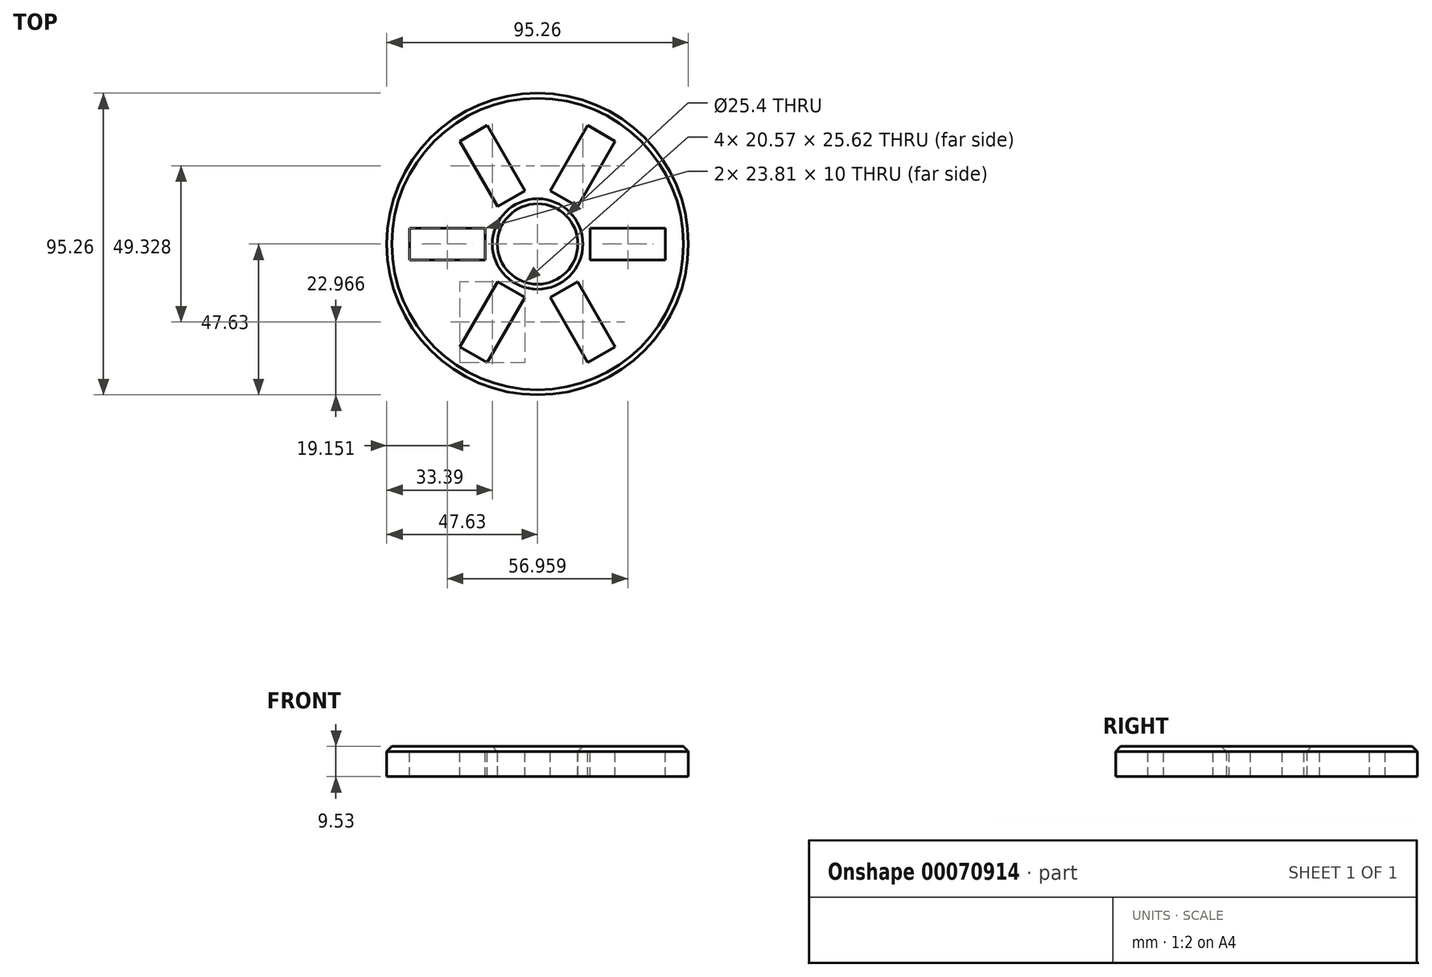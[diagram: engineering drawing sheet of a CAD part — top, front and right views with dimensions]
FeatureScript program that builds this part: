
annotation { "Feature Type Name" : "Feature", "Feature Type Description" : "" }
export const myFeature = defineFeature(function(context is Context, id is Id, definition is map)
    precondition{}
    {
        {
            var Q0;
            Q0=qCreatedBy(makeId("Top.planeOp"),FACE);
            var sketch = newSketch(context, id + "F0", { "sketchPlane" : qUnion([Q0])});
            skCircle(sketch, "E0", {"center": v(0, 0) * mm, "radius": 47.63 * mm});
            skCircle(sketch, "E1", {"center": v(0, 0) * mm, "radius": 12.7 * mm});
            skSolve(sketch);
        }
        {
            var Q0;
            Q0=makeQuery(id+"F0.imprint","IMPRINT",FACE,{"disambiguationData":[TD([[makeQuery(id+"F0.imprint","IMPRINT",EDGE,{"derivedFrom":sQuery(id+"F0.wireOp",EDGE,"E0")}),1.0]])]});
            extrude(context, id + "F1", {"entities" : qUnion([Q0]), "depth" : 9.52 * mm});
        }
        {
            var Q0;
            Q0=makeQuery(id+"F1.opExtrude","CAP_FACE",FACE,{"disambiguationData":[OSD([sQuery(id+"F0.wireOp",EDGE,"E0"),sQuery(id+"F0.wireOp",EDGE,"E1")])],"isStart":false});
            var sketch = newSketch(context, id + "F2", { "sketchPlane" : qUnion([Q0])});
            skLineSegment(sketch, "E2.rect.bottom", {"start": v(-16.57, -5) * mm, "end": v(-40.39, -5) * mm});
            skLineSegment(sketch, "E2.rect.top", {"start": v(-16.57, 5) * mm, "end": v(-40.39, 5) * mm});
            skLineSegment(sketch, "E2.rect.left", {"start": v(-16.57, -5) * mm, "end": v(-16.57, 5) * mm});
            skLineSegment(sketch, "E2.rect.right", {"start": v(-40.39, -5) * mm, "end": v(-40.39, 5) * mm});
            skPoint(sketch, "E2.rect.middle", {"position": v(-28.48, 0) * mm});
            skLineSegment(sketch, "E3", {"start": v(-47.63, 0) * mm, "end": v(-12.7, 0) * mm, "construction": true});
            skPoint(sketch, "E3.startSnap0", {"position": v(-40.39, 0) * mm});
            skPoint(sketch, "E3.endSnap0", {"position": v(-16.57, 0) * mm});
            skLineSegment(sketch, "E4.1.0", {"start": v(-12.62, -11.85) * mm, "end": v(-24.52, -32.48) * mm});
            skLineSegment(sketch, "E4.1.1", {"start": v(-3.96, -16.85) * mm, "end": v(-15.86, -37.48) * mm});
            skLineSegment(sketch, "E4.1.2", {"start": v(-3.96, -16.85) * mm, "end": v(-12.62, -11.85) * mm});
            skLineSegment(sketch, "E4.1.3", {"start": v(-15.86, -37.48) * mm, "end": v(-24.52, -32.48) * mm});
            skLineSegment(sketch, "E4.2.0", {"start": v(3.96, -16.85) * mm, "end": v(15.86, -37.48) * mm});
            skLineSegment(sketch, "E4.2.1", {"start": v(12.62, -11.85) * mm, "end": v(24.52, -32.48) * mm});
            skLineSegment(sketch, "E4.2.2", {"start": v(12.62, -11.85) * mm, "end": v(3.96, -16.85) * mm});
            skLineSegment(sketch, "E4.2.3", {"start": v(24.52, -32.48) * mm, "end": v(15.86, -37.48) * mm});
            skLineSegment(sketch, "E4.3.0", {"start": v(16.57, -5) * mm, "end": v(40.39, -5) * mm});
            skLineSegment(sketch, "E4.3.1", {"start": v(16.57, 5) * mm, "end": v(40.39, 5) * mm});
            skLineSegment(sketch, "E4.3.2", {"start": v(16.57, 5) * mm, "end": v(16.57, -5) * mm});
            skLineSegment(sketch, "E4.3.3", {"start": v(40.39, 5) * mm, "end": v(40.39, -5) * mm});
            skLineSegment(sketch, "E4.4.0", {"start": v(12.62, 11.85) * mm, "end": v(24.52, 32.48) * mm});
            skLineSegment(sketch, "E4.4.1", {"start": v(3.96, 16.85) * mm, "end": v(15.86, 37.48) * mm});
            skLineSegment(sketch, "E4.4.2", {"start": v(3.96, 16.85) * mm, "end": v(12.62, 11.85) * mm});
            skLineSegment(sketch, "E4.4.3", {"start": v(15.86, 37.48) * mm, "end": v(24.52, 32.48) * mm});
            skLineSegment(sketch, "E4.5.0", {"start": v(-3.96, 16.85) * mm, "end": v(-15.86, 37.48) * mm});
            skLineSegment(sketch, "E4.5.1", {"start": v(-12.62, 11.85) * mm, "end": v(-24.52, 32.48) * mm});
            skLineSegment(sketch, "E4.5.2", {"start": v(-12.62, 11.85) * mm, "end": v(-3.96, 16.85) * mm});
            skLineSegment(sketch, "E4.5.3", {"start": v(-24.52, 32.48) * mm, "end": v(-15.86, 37.48) * mm});
            skPoint(sketch, "E4.center", {"position": v(0, 0) * mm});
            skSolve(sketch);
        }
        {
            var Q0;
            Q0=makeQuery(id+"F2.imprint","IMPRINT",FACE,{"disambiguationData":[TD([[makeQuery(id+"F2.imprint","IMPRINT",EDGE,{"derivedFrom":sQuery(id+"F2.wireOp",EDGE,"E2.rect.bottom")}),-1.0]])]});
            var Q1;
            Q1=makeQuery(id+"F2.imprint","IMPRINT",FACE,{"disambiguationData":[TD([[makeQuery(id+"F2.imprint","IMPRINT",EDGE,{"derivedFrom":sQuery(id+"F2.wireOp",EDGE,"E4.5.0")}),1.0]])]});
            var Q2;
            Q2=makeQuery(id+"F2.imprint","IMPRINT",FACE,{"disambiguationData":[TD([[makeQuery(id+"F2.imprint","IMPRINT",EDGE,{"derivedFrom":sQuery(id+"F2.wireOp",EDGE,"E4.4.0")}),1.0]])]});
            var Q3;
            Q3=makeQuery(id+"F2.imprint","IMPRINT",FACE,{"disambiguationData":[TD([[makeQuery(id+"F2.imprint","IMPRINT",EDGE,{"derivedFrom":sQuery(id+"F2.wireOp",EDGE,"E4.3.0")}),1.0]])]});
            var Q4;
            Q4=makeQuery(id+"F2.imprint","IMPRINT",FACE,{"disambiguationData":[TD([[makeQuery(id+"F2.imprint","IMPRINT",EDGE,{"derivedFrom":sQuery(id+"F2.wireOp",EDGE,"E4.2.0")}),1.0]])]});
            var Q5;
            Q5=makeQuery(id+"F2.imprint","IMPRINT",FACE,{"disambiguationData":[TD([[makeQuery(id+"F2.imprint","IMPRINT",EDGE,{"derivedFrom":sQuery(id+"F2.wireOp",EDGE,"E4.1.0")}),1.0]])]});
            extrude(context, id + "F3", {"entities" : qUnion([Q0, Q1, Q2, Q3, Q4, Q5]), "operationType" : NewBodyOperationType.REMOVE, "endBound" : BoundingType.THROUGH_ALL, "oppositeDirection" : true, "depth" : 6.35 * mm});
        }
        {
            var Q0;
            Q0=makeQuery(id+"F3.boolean.opBoolean","COPY",EDGE,{"derivedFrom":makeQuery(id+"F3.opExtrude","CAP_EDGE",EDGE,{"disambiguationData":[OSD([sQuery(id+"F2.wireOp",EDGE,"E2.rect.top")])],"isStart":true})});
            var Q1;
            Q1=makeQuery(id+"F3.boolean.opBoolean","COPY",EDGE,{"derivedFrom":makeQuery(id+"F3.opExtrude","CAP_EDGE",EDGE,{"disambiguationData":[OSD([sQuery(id+"F2.wireOp",EDGE,"E2.rect.right")])],"isStart":true})});
            var Q2;
            Q2=makeQuery(id+"F3.boolean.opBoolean","COPY",EDGE,{"derivedFrom":makeQuery(id+"F3.opExtrude","CAP_EDGE",EDGE,{"disambiguationData":[OSD([sQuery(id+"F2.wireOp",EDGE,"E2.rect.bottom")])],"isStart":true})});
            var Q3;
            Q3=makeQuery(id+"F3.boolean.opBoolean","COPY",EDGE,{"derivedFrom":makeQuery(id+"F3.opExtrude","CAP_EDGE",EDGE,{"disambiguationData":[OSD([sQuery(id+"F2.wireOp",EDGE,"E2.rect.left")])],"isStart":true})});
            var Q4;
            Q4=makeQuery(id+"F1.opExtrude","CAP_EDGE",EDGE,{"disambiguationData":[OSD([sQuery(id+"F0.wireOp",EDGE,"E1")])],"isStart":false});
            var Q5;
            Q5=makeQuery(id+"F3.boolean.opBoolean","COPY",EDGE,{"derivedFrom":makeQuery(id+"F3.opExtrude","CAP_EDGE",EDGE,{"disambiguationData":[OSD([sQuery(id+"F2.wireOp",EDGE,"E4.5.2")])],"isStart":true})});
            var Q6;
            Q6=makeQuery(id+"F3.boolean.opBoolean","COPY",EDGE,{"derivedFrom":makeQuery(id+"F3.opExtrude","CAP_EDGE",EDGE,{"disambiguationData":[OSD([sQuery(id+"F2.wireOp",EDGE,"E4.5.1")])],"isStart":true})});
            var Q7;
            Q7=makeQuery(id+"F3.boolean.opBoolean","COPY",EDGE,{"derivedFrom":makeQuery(id+"F3.opExtrude","CAP_EDGE",EDGE,{"disambiguationData":[OSD([sQuery(id+"F2.wireOp",EDGE,"E4.5.0")])],"isStart":true})});
            var Q8;
            Q8=makeQuery(id+"F3.boolean.opBoolean","COPY",EDGE,{"derivedFrom":makeQuery(id+"F3.opExtrude","CAP_EDGE",EDGE,{"disambiguationData":[OSD([sQuery(id+"F2.wireOp",EDGE,"E4.5.3")])],"isStart":true})});
            var Q9;
            Q9=makeQuery(id+"F3.boolean.opBoolean","COPY",EDGE,{"derivedFrom":makeQuery(id+"F3.opExtrude","CAP_EDGE",EDGE,{"disambiguationData":[OSD([sQuery(id+"F2.wireOp",EDGE,"E4.4.1")])],"isStart":true})});
            var Q10;
            Q10=makeQuery(id+"F3.boolean.opBoolean","COPY",EDGE,{"derivedFrom":makeQuery(id+"F3.opExtrude","CAP_EDGE",EDGE,{"disambiguationData":[OSD([sQuery(id+"F2.wireOp",EDGE,"E4.4.3")])],"isStart":true})});
            var Q11;
            Q11=makeQuery(id+"F3.boolean.opBoolean","COPY",EDGE,{"derivedFrom":makeQuery(id+"F3.opExtrude","CAP_EDGE",EDGE,{"disambiguationData":[OSD([sQuery(id+"F2.wireOp",EDGE,"E4.4.2")])],"isStart":true})});
            var Q12;
            Q12=makeQuery(id+"F3.boolean.opBoolean","COPY",EDGE,{"derivedFrom":makeQuery(id+"F3.opExtrude","CAP_EDGE",EDGE,{"disambiguationData":[OSD([sQuery(id+"F2.wireOp",EDGE,"E4.4.0")])],"isStart":true})});
            var Q13;
            Q13=makeQuery(id+"F3.boolean.opBoolean","COPY",EDGE,{"derivedFrom":makeQuery(id+"F3.opExtrude","CAP_EDGE",EDGE,{"disambiguationData":[OSD([sQuery(id+"F2.wireOp",EDGE,"E4.3.2")])],"isStart":true})});
            var Q14;
            Q14=makeQuery(id+"F3.boolean.opBoolean","COPY",EDGE,{"derivedFrom":makeQuery(id+"F3.opExtrude","CAP_EDGE",EDGE,{"disambiguationData":[OSD([sQuery(id+"F2.wireOp",EDGE,"E4.3.1")])],"isStart":true})});
            var Q15;
            Q15=makeQuery(id+"F3.boolean.opBoolean","COPY",EDGE,{"derivedFrom":makeQuery(id+"F3.opExtrude","CAP_EDGE",EDGE,{"disambiguationData":[OSD([sQuery(id+"F2.wireOp",EDGE,"E4.3.3")])],"isStart":true})});
            var Q16;
            Q16=makeQuery(id+"F3.boolean.opBoolean","COPY",EDGE,{"derivedFrom":makeQuery(id+"F3.opExtrude","CAP_EDGE",EDGE,{"disambiguationData":[OSD([sQuery(id+"F2.wireOp",EDGE,"E4.3.0")])],"isStart":true})});
            var Q17;
            Q17=makeQuery(id+"F3.boolean.opBoolean","COPY",EDGE,{"derivedFrom":makeQuery(id+"F3.opExtrude","CAP_EDGE",EDGE,{"disambiguationData":[OSD([sQuery(id+"F2.wireOp",EDGE,"E4.2.1")])],"isStart":true})});
            var Q18;
            Q18=makeQuery(id+"F3.boolean.opBoolean","COPY",EDGE,{"derivedFrom":makeQuery(id+"F3.opExtrude","CAP_EDGE",EDGE,{"disambiguationData":[OSD([sQuery(id+"F2.wireOp",EDGE,"E4.2.2")])],"isStart":true})});
            var Q19;
            Q19=makeQuery(id+"F3.boolean.opBoolean","COPY",EDGE,{"derivedFrom":makeQuery(id+"F3.opExtrude","CAP_EDGE",EDGE,{"disambiguationData":[OSD([sQuery(id+"F2.wireOp",EDGE,"E4.2.0")])],"isStart":true})});
            var Q20;
            Q20=makeQuery(id+"F3.boolean.opBoolean","COPY",EDGE,{"derivedFrom":makeQuery(id+"F3.opExtrude","CAP_EDGE",EDGE,{"disambiguationData":[OSD([sQuery(id+"F2.wireOp",EDGE,"E4.2.3")])],"isStart":true})});
            var Q21;
            Q21=makeQuery(id+"F3.boolean.opBoolean","COPY",EDGE,{"derivedFrom":makeQuery(id+"F3.opExtrude","CAP_EDGE",EDGE,{"disambiguationData":[OSD([sQuery(id+"F2.wireOp",EDGE,"E4.1.1")])],"isStart":true})});
            var Q22;
            Q22=makeQuery(id+"F3.boolean.opBoolean","COPY",EDGE,{"derivedFrom":makeQuery(id+"F3.opExtrude","CAP_EDGE",EDGE,{"disambiguationData":[OSD([sQuery(id+"F2.wireOp",EDGE,"E4.1.3")])],"isStart":true})});
            var Q23;
            Q23=makeQuery(id+"F3.boolean.opBoolean","COPY",EDGE,{"derivedFrom":makeQuery(id+"F3.opExtrude","CAP_EDGE",EDGE,{"disambiguationData":[OSD([sQuery(id+"F2.wireOp",EDGE,"E4.1.0")])],"isStart":true})});
            var Q24;
            Q24=makeQuery(id+"F3.boolean.opBoolean","COPY",EDGE,{"derivedFrom":makeQuery(id+"F3.opExtrude","CAP_EDGE",EDGE,{"disambiguationData":[OSD([sQuery(id+"F2.wireOp",EDGE,"E4.1.2")])],"isStart":true})});
            var Q25;
            Q25=makeQuery(id+"F1.opExtrude","CAP_EDGE",EDGE,{"disambiguationData":[OSD([sQuery(id+"F0.wireOp",EDGE,"E0")])],"isStart":false});
            chamfer(context, id + "F4", {"entities" : qUnion([Q0, Q1, Q2, Q3, Q4, Q5, Q6, Q7, Q8, Q9, Q10, Q11, Q12, Q13, Q14, Q15, Q16, Q17, Q18, Q19, Q20, Q21, Q22, Q23, Q24, Q25]), "width" : 1.59 * mm, "tangentPropagation" : true});
        }
    });
